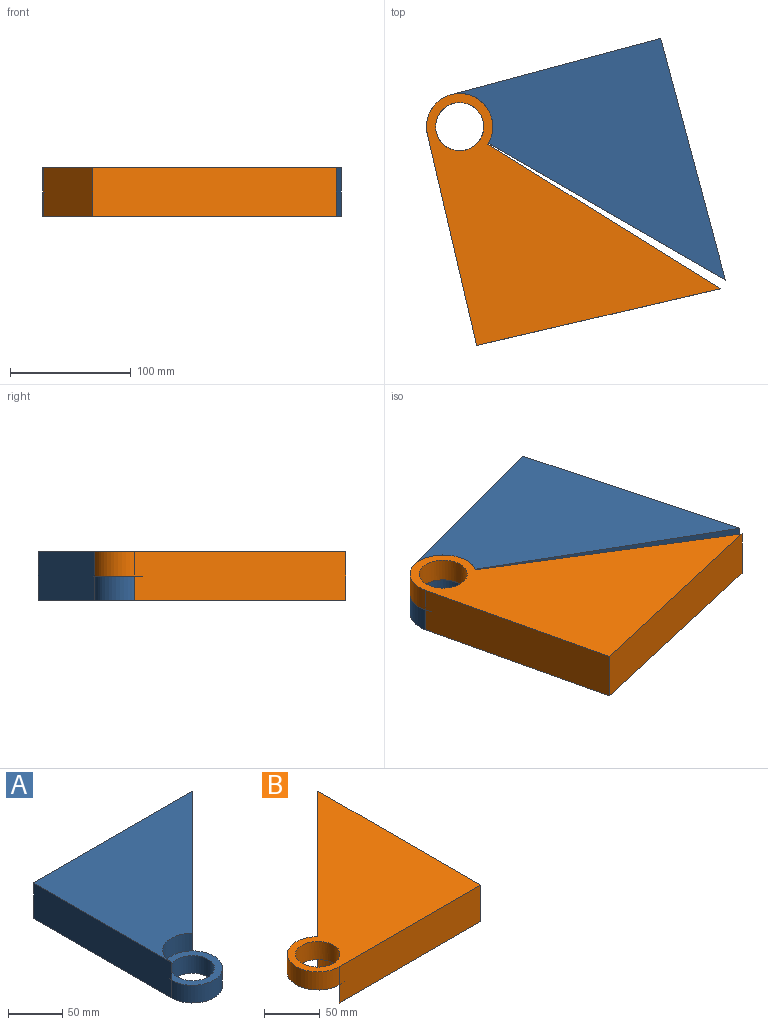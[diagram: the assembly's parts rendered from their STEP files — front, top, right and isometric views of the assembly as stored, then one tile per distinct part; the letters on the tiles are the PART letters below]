
ASSEMBLY  parts=2 mates=1
PART A: 9 faces, bbox 207.5x207.5x40 mm
  f0: cylinder r=27.5mm len=55mm, axis (0,0,-1), area 2159.8mm2, adj f2,f3,f6,f8
  f1: cylinder r=20mm len=40mm, axis (0,0,-1), area 2513.3mm2, adj f6,f8
  f2: plane 180x40mm, normal (-1,0,0), area 7200mm2, adj f0,f4,f5,f6,f7
  f3: plane 160.55x160.55mm, normal (0.71,-0.71,0), area 9082.3mm2, adj f0,f4,f5,f6,f7
  f4: plane 207.5x40mm, normal (0,1,0), area 8300mm2, adj f2,f3,f5,f6
  f5: plane 207.5x180mm, normal (0,0,1), area 20259.1mm2, adj f2,f3,f4,f7
  f6: plane 207.5x207.5mm, normal (0,0,-1), area 21378.3mm2, adj f0,f1,f2,f3,f4
  f7: cylinder r=27.5mm len=46.95mm, axis (0,0,1), area 1295.9mm2, adj f2,f3,f5,f8
  f8: plane 55x55mm, normal (0,0,1), area 1119.2mm2, adj f0,f1,f7
PART B: 9 faces, bbox 207.5x207.5x40 mm
  f0: cylinder r=20mm len=40mm, axis (0,0,-1), area 2513.3mm2, adj f5,f8
  f1: plane 180x40mm, normal (0,-1,0), area 7200mm2, adj f2,f4,f5,f6,f7
  f2: plane 207.5x40mm, normal (1,0,0), area 8300mm2, adj f1,f3,f5,f6
  f3: plane 160.55x160.55mm, normal (-0.71,0.71,0), area 9082.3mm2, adj f2,f4,f5,f6,f7
  f4: cylinder r=27.5mm len=55mm, axis (0,0,-1), area 2159.8mm2, adj f1,f3,f5,f8
  f5: plane 207.5x207.5mm, normal (0,0,1), area 21378.3mm2, adj f0,f1,f2,f3,f4
  f6: plane 207.5x180mm, normal (0,0,-1), area 20259.1mm2, adj f1,f2,f3,f7
  f7: cylinder r=27.5mm len=46.95mm, axis (0,0,-1), area 1295.9mm2, adj f1,f3,f6,f8
  f8: plane 55x55mm, normal (0,0,-1), area 1119.2mm2, adj f0,f4,f7
PLACE A rot(axis=(0,0,-1),75deg) t=(-67.18,323.14,20.37)mm
PLACE B rot(axis=(0,0,-1),76.9deg) t=(-30.9,250.91,20.37)mm
MATE cylindrical B.f0 <-> A.f1  axis (0,0,1) through (-67.18,323.14,60.37)mm
